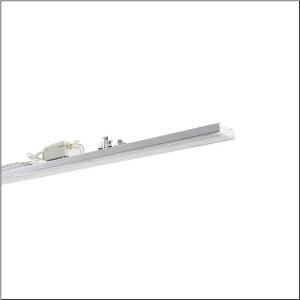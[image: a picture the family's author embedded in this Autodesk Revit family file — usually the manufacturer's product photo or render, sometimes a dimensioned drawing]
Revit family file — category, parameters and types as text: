
# Revit family: licross_r__21_recessed_mo_52tl12dn47xg_42f8
name_source: partatom
category: Lighting Fixtures
units: mm (PartAtom-declared; Revit-internal decimal feet)

## family parameters
Cut with Voids When Loaded = No
Host = Face
Light Source = No
Part Type = Normal
Room Calculation Point = No
Round Connector Dimension = Use Diameter
Shared = No

## types (1)
- --- (1 x LED, 7230 lm, 39.3 W, 4000K)
    Apparent Load = 39 VA
    CIE Flux Codes = 72 92 99 100 100
    Color Rendering = 80
    Color Temperature = 4000K
    Default Elevation = 1800 mm
    Description = Licross® 21 Recessed MO, luminaire insert, of sheet steel, galvanised, coil coated, white, length: 1.500mm, width: 66mm, height: 67mm, LED rated luminous flux: 7.230lm, light colour: 840, control gear: DALI 2, with plug, 5-pole, with phase selection, mains connection: 220..240V, AC, 50/60Hz, rated input power: 39W, halogen-free wiring, primary optical cover: cover, of PMMA, light emission: direct distribution, primary light characteristic: symmetric, protection rating (complete): IP40, insulation class (complete): insulation class I (protective earthing), certification: CE, ENEC, VDE, UKCA, protection symbol: D if used in an environment without relevant dust loads with corresponding accessories, impact resistance: IK06, permissible ambient temperature for indoor applications: -25..+40°C, corresponds to IFS (International Featured Standards) requirements for safety and quality in the food industry, reducing of maximum allowable ambient temperature of 5°C with ceiling mounting, LABS conformity tested according to VDMA 24364:2018-05, packaging unit: 1 piece
    Height = 58 mm
    Lamp = 1 x LED
    Lamp Light Flux = 7230 lm
    Lamp Power = 39.3 W
    Lamp count = 1
    Length = 1500 mm
    Luminous efficacy = 184 lm/W
    Manufacturer = Siteco
    ModVariant = No
    Model = 52TL12DN47XG
    Mounting Place = Ceiling
    Mounting Type = Pendant
    Number of Poles = 1
    OnlyDefault = Yes
    Power Factor = 1
    Product Name = Licross® 21 Recessed MO
    Product group = luminaire insert
    ProductGroupID = 901
    Protection Class = Protection class I
    Protection Degree = IP 40
    RLX_Detail_Level = 1
    RLX_Emergency_Light_Flux = 0 lm
    RLX_Emergency_Type = 0
    RLX_Emergency_Type_DB = No
    RlxData = <blob elided: 24209 chars, md5=60235539>
    Socket = socket
    Standby Power = 0 W
    System Light Flux = 7230 lm
    System Power = 39 W
    Type Comments = factory setting: luminous flux: 100 % | dim-lin: 254 | 267 mA
    Type Image = l_1296930.jpg
    URL = http://relux.com
    VarID = @adj_057825
    Voltage = 0 V
    Weight = 0.00 kg
    Width = 66 mm

## geometry (parser evidence)
native form markers: Blend x4, Sweep x11
no freeform markers — native parametric forms only
